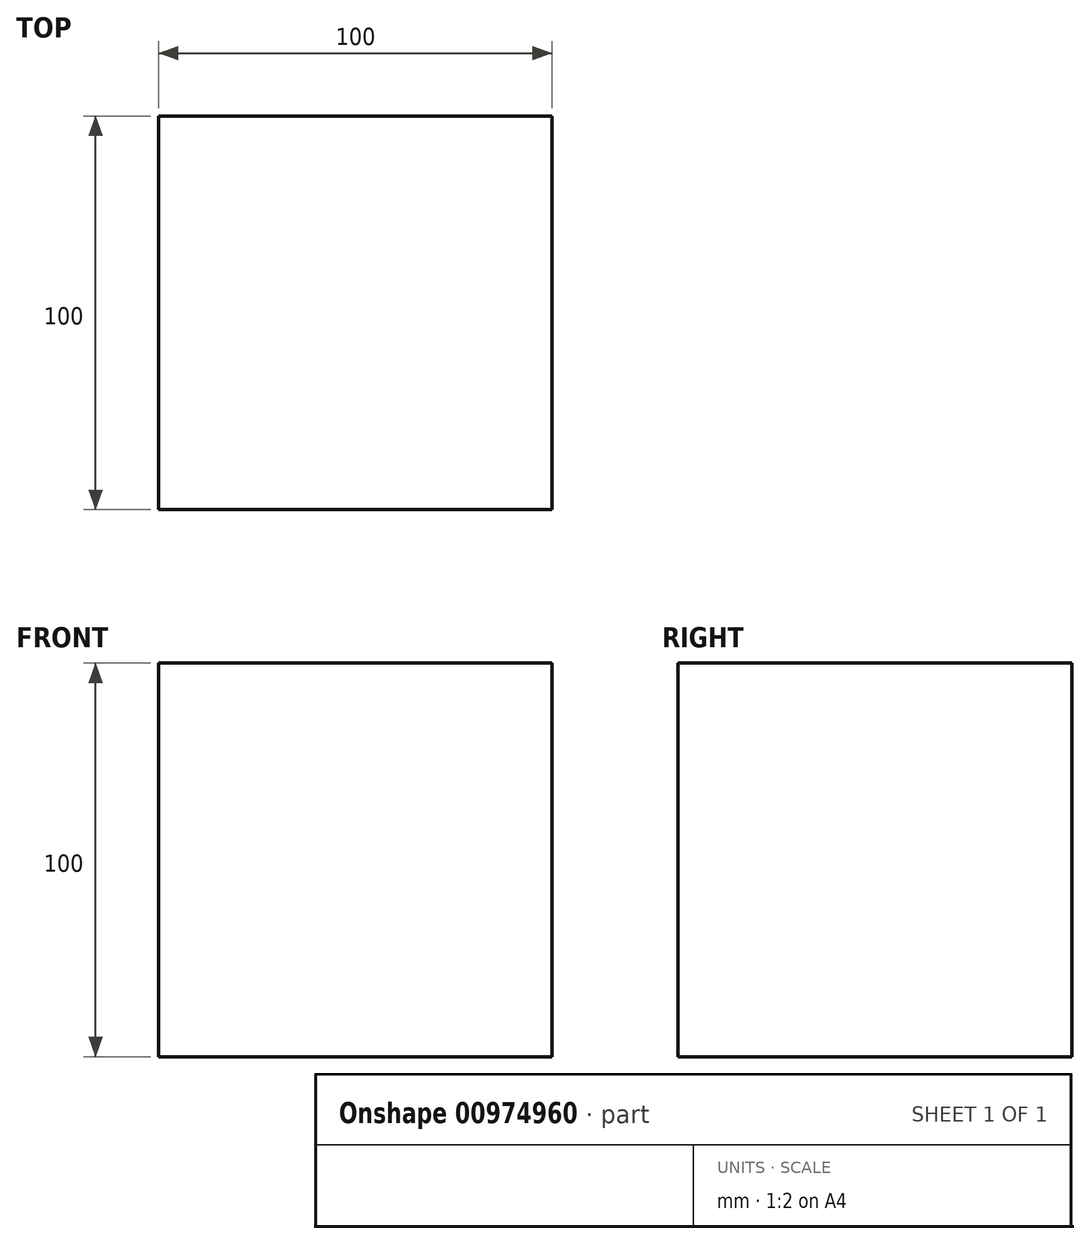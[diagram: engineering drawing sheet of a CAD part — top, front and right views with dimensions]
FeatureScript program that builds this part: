
annotation { "Feature Type Name" : "Feature", "Feature Type Description" : "" }
export const myFeature = defineFeature(function(context is Context, id is Id, definition is map)
    precondition{}
    {
        {
            var Q0;
            Q0=qCreatedBy(makeId("Front.planeOp"),FACE);
            var sketch = newSketch(context, id + "F0", { "sketchPlane" : qUnion([Q0])});
            skLineSegment(sketch, "E0.bottom", {"start": v(50, 50) * mm, "end": v(-50, 50) * mm});
            skLineSegment(sketch, "E0.top", {"start": v(50, -50) * mm, "end": v(-50, -50) * mm});
            skLineSegment(sketch, "E0.left", {"start": v(50, 50) * mm, "end": v(50, -50) * mm});
            skLineSegment(sketch, "E0.right", {"start": v(-50, 50) * mm, "end": v(-50, -50) * mm});
            skPoint(sketch, "E0.middle", {"position": v(0, 0) * mm});
            skSolve(sketch);
        }
        {
            var Q0;
            Q0 = qSketchRegion(id + "F0", true);
            extrude(context, id + "F1", {"entities" : qUnion([Q0]), "endBound" : BoundingType.SYMMETRIC, "depth" : 100 * mm, "offsetDistance" : 25 * mm});
        }
    });
